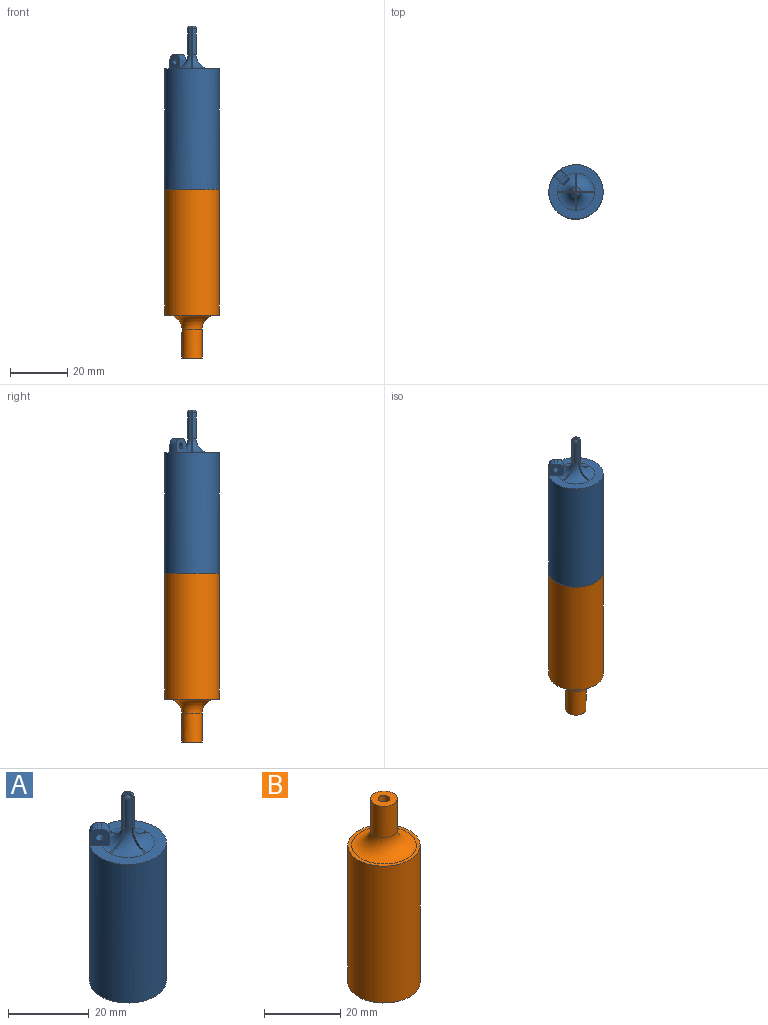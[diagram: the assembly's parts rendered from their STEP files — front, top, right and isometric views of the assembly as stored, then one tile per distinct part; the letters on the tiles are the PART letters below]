
ASSEMBLY  parts=2 mates=1
PART A: 36 faces, bbox 21.9x21.9x57.2 mm
  f0: plane 19x19mm, normal (0,0,1), area 154.5mm2, adj f1,f3,f4,f8,f9,f11,f13,f15
  f1: cylinder r=9.5mm len=45mm, axis (0,0,-1), area 2516mm2, adj f0,f2,f25,f27,f30
  f2: plane 19x19mm, normal (0,0,-1), area 106.8mm2, adj f1,f23
  f3: plane 15.15x6.4mm, normal (-1,0,0), area 23.6mm2, adj f0,f4,f5,f6,f22,f35
  f4: plane 15.15x6.4mm, normal (0,-1,0), area 23.6mm2, adj f0,f3,f5,f6,f22,f35
  f5: cylinder r=1.5mm len=9mm, axis (0,0,-1), area 16.7mm2, adj f3,f4,f22,f35
  f6: plane 0.18x0.18mm, normal (0,0,1), area 0mm2, adj f3,f4,f22
  f7: cylinder r=1.5mm len=9mm, axis (0,0,-1), area 16.7mm2, adj f8,f9,f21,f34
  f8: plane 15.15x6.4mm, normal (0,-1,0), area 23.6mm2, adj f0,f7,f9,f10,f21,f34
  f9: plane 15.15x6.4mm, normal (1,0,0), area 23.6mm2, adj f0,f7,f8,f10,f21,f34
  f10: plane 0.18x0.18mm, normal (0,0,1), area 0mm2, adj f8,f9,f21
  f11: plane 15.15x6.4mm, normal (0,1,0), area 23.6mm2, adj f0,f12,f13,f14,f20,f33
  f12: cylinder r=1.5mm len=9mm, axis (0,0,-1), area 16.7mm2, adj f11,f13,f20,f33
  f13: plane 15.15x6.4mm, normal (1,0,0), area 23.6mm2, adj f0,f11,f12,f14,f20,f33
  f14: plane 0.18x0.18mm, normal (0,0,1), area 0mm2, adj f11,f13,f20
  f15: plane 15.15x6.4mm, normal (0,1,0), area 23.6mm2, adj f0,f16,f17,f18,f19,f32
  f16: plane 15.15x6.4mm, normal (-1,0,0), area 23.6mm2, adj f0,f15,f17,f18,f19,f32
  f17: cylinder r=1.5mm len=9mm, axis (0,0,-1), area 16.7mm2, adj f15,f16,f19,f32
  f18: plane 0.18x0.18mm, normal (0,0,1), area 0mm2, adj f15,f16,f19
  f19: torus R=0.5mm, axis (0,0,1), area 2mm2, adj f15,f16,f17,f18
  f20: torus R=0.5mm, axis (0,0,1), area 2mm2, adj f11,f12,f13,f14
  f21: torus R=0.5mm, axis (0,0,1), area 2mm2, adj f7,f8,f9,f10
  f22: torus R=0.5mm, axis (0,0,1), area 2mm2, adj f3,f4,f5,f6
  f23: cylinder r=7.5mm len=40mm, axis (0,0,-1), area 1885mm2, adj f2,f24
  f24: plane 15x15mm, normal (0,0,-1), area 176.7mm2, adj f23
  f25: plane 5.19x3.64mm, normal (-0.71,-0.71,0), area 19.3mm2, adj f0,f1,f26,f28,f29,f30,f31,f34
  f26: plane 2.68x2.12mm, normal (0.71,-0.71,0), area 7.9mm2, adj f25,f27,f29,f34
  f27: plane 5.19x3.64mm, normal (0.71,0.71,0), area 19.3mm2, adj f0,f1,f26,f28,f29,f30,f31,f34
  f28: plane 2.72x2.72mm, normal (0,0,1), area 2.8mm2, adj f25,f27,f29,f30
  f29: cylinder r=2mm len=3.54mm, axis (-0.71,-0.71,0), area 9.4mm2, adj f25,f26,f27,f28
  f30: torus R=7.5mm, axis (0,0,1), area 9.9mm2, adj f1,f25,f27,f28
  f31: cylinder r=1mm len=3.54mm, axis (0.71,0.71,0), area 18.8mm2, adj f25,f27
  f32: torus R=6.5mm, axis (0,0,1), area 36.4mm2, adj f0,f15,f16,f17
  f33: torus R=6.5mm, axis (0,0,1), area 36.4mm2, adj f0,f11,f12,f13
  f34: torus R=6.5mm, axis (0,0,1), area 30.4mm2, adj f0,f7,f8,f9,f25,f26,f27
  f35: torus R=6.5mm, axis (0,0,1), area 36.4mm2, adj f0,f3,f4,f5
PART B: 10 faces, bbox 19x19x59 mm
  f0: cylinder r=3.5mm len=10mm, axis (0,0,-1), area 219.9mm2, adj f1,f7
  f1: plane 7x7mm, normal (0,0,1), area 31.4mm2, adj f0,f8
  f2: cylinder r=9.5mm len=44mm, axis (0,0,1), area 2626.4mm2, adj f3,f4
  f3: plane 19x19mm, normal (0,0,-1), area 106.8mm2, adj f2,f5
  f4: plane 19x19mm, normal (0,0,1), area 56.5mm2, adj f2,f7
  f5: cylinder r=7.5mm len=42mm, axis (0,0,-1), area 1979.2mm2, adj f3,f6
  f6: plane 15x15mm, normal (0,0,-1), area 176.7mm2, adj f5
  f7: torus R=8.5mm, axis (0,0,-1), area 262.4mm2, adj f0,f4
  f8: cylinder r=1.5mm len=10mm, axis (0,0,1), area 94.2mm2, adj f1,f9
  f9: plane 3x3mm, normal (0,0,1), area 7.1mm2, adj f8
PLACE A at identity
PLACE B rot(axis=(0,1,0),180deg) t=(0,0,-44)mm
MATE fastened B.f2 <-> A.f5  axis (0,0,1) through (0,0,0)mm
